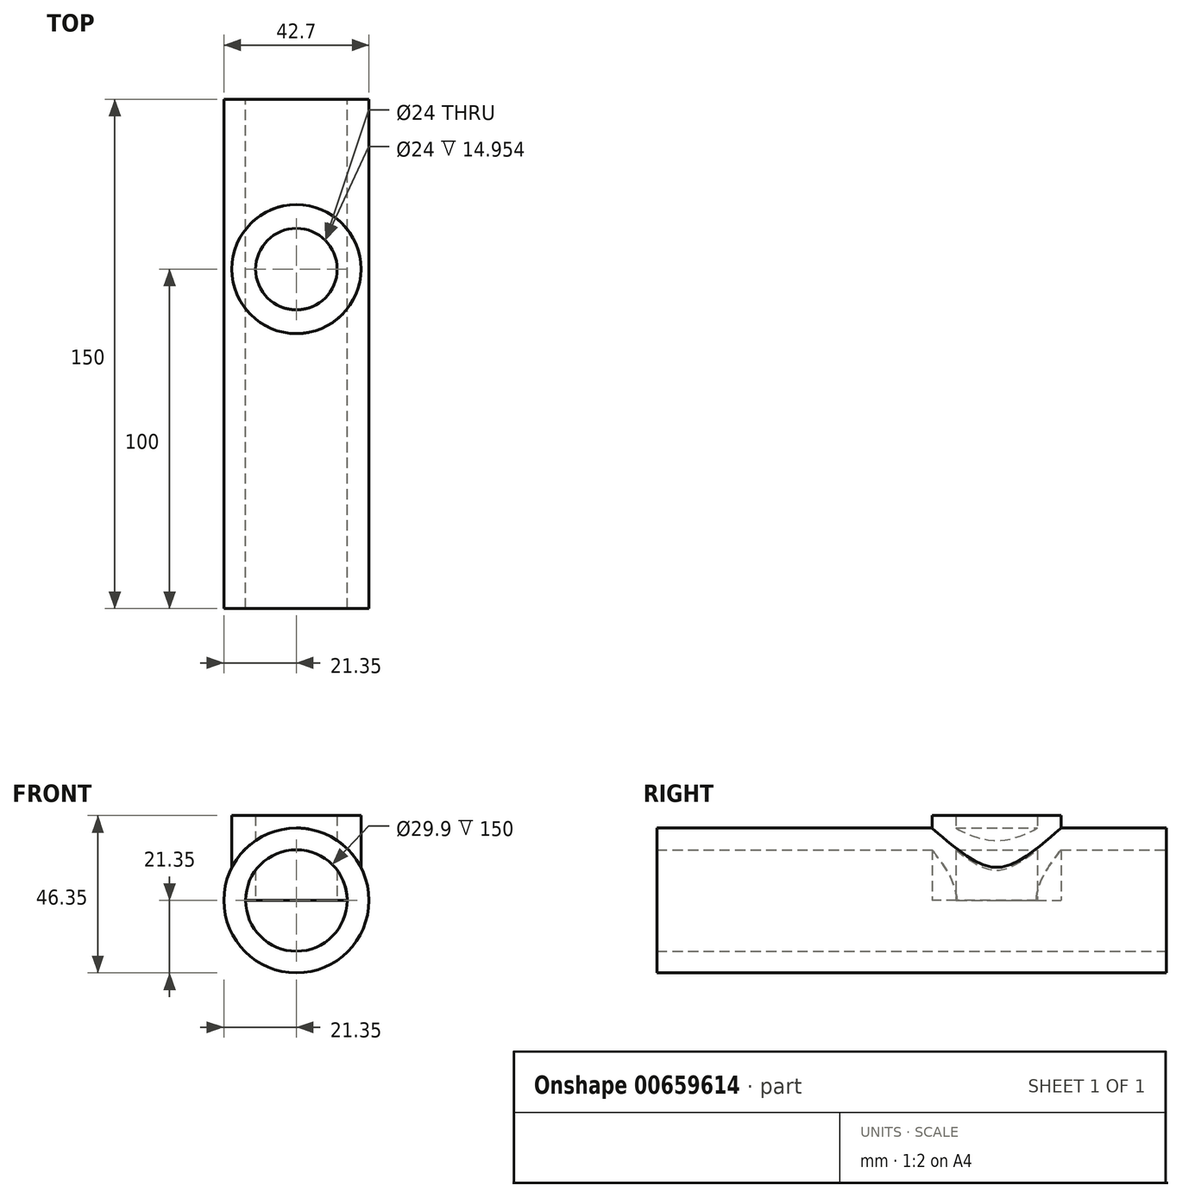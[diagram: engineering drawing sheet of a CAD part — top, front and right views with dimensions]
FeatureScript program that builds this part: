
annotation { "Feature Type Name" : "Feature", "Feature Type Description" : "" }
export const myFeature = defineFeature(function(context is Context, id is Id, definition is map)
    precondition{}
    {
        {
            var Q0;
            Q0=qCreatedBy(makeId("Front.planeOp"),FACE);
            var sketch = newSketch(context, id + "F0", { "sketchPlane" : qUnion([Q0])});
            skCircle(sketch, "E0", {"center": v(0, 0) * mm, "radius": 21.35 * mm});
            skCircle(sketch, "E1", {"center": v(0, 0) * mm, "radius": 14.95 * mm});
            skCircle(sketch, "E2", {"center": v(186.86, -2.46) * mm, "radius": 20.6 * mm});
            skSolve(sketch);
        }
        {
            var Q0;
            Q0=makeQuery(id+"F0.imprint","IMPRINT",FACE,{"disambiguationData":[TD([[makeQuery(id+"F0.imprint","IMPRINT",EDGE,{"derivedFrom":sQuery(id+"F0.wireOp",EDGE,"E0")}),1.0]])]});
            extrude(context, id + "F1", {"entities" : qUnion([Q0]), "depth" : 100 * mm, "offsetDistance" : 25 * mm});
        }
        {
            var Q0;
            Q0=makeQuery(id+"F1.opExtrude","CAP_FACE",FACE,{"disambiguationData":[OSD([sQuery(id+"F0.wireOp",EDGE,"E0"),sQuery(id+"F0.wireOp",EDGE,"E1")])],"isStart":true});
            extrude(context, id + "F2", {"entities" : qUnion([Q0]), "operationType" : NewBodyOperationType.ADD, "depth" : 50 * mm, "offsetDistance" : 25 * mm});
        }
        {
            var Q0;
            Q0=qCreatedBy(makeId("Top.planeOp"),FACE);
            var sketch = newSketch(context, id + "F3", { "sketchPlane" : qUnion([Q0])});
            skCircle(sketch, "E3", {"center": v(0, 0) * mm, "radius": 19 * mm});
            skCircle(sketch, "E4", {"center": v(0, 0) * mm, "radius": 12 * mm});
            skSolve(sketch);
        }
        {
            var Q0;
            Q0 = qSketchRegion(id + "F3", true);
            extrude(context, id + "F4", {"entities" : qUnion([Q0]), "operationType" : NewBodyOperationType.ADD, "depth" : 25 * mm, "offsetDistance" : 25 * mm});
        }
        {
            var Q0;
            Q0=makeQuery(id+"F1.opExtrude","SWEPT_BODY",BODY,{"disambiguationData":[OSD([sQuery(id+"F0.wireOp",EDGE,"E0"),sQuery(id+"F0.wireOp",EDGE,"E1")])]});
            transform(context, id + "F5", {"entities" : qUnion([Q0]), "transformType" : TransformType.TRANSLATION_3D, "dx" : 200 * mm, "dy" : 0 * mm, "dz" : 0 * mm, "makeCopy" : true});
        }
        {
            var Q0;
            Q0=makeQuery(id+"F5.opPattern","COPY",FACE,{"derivedFrom":makeQuery(id+"F1.opExtrude","CAP_FACE",FACE,{"disambiguationData":[OSD([sQuery(id+"F0.wireOp",EDGE,"E0"),sQuery(id+"F0.wireOp",EDGE,"E1")])],"isStart":false}),"instanceName":"1"});
            extrude(context, id + "F6", {"entities" : qUnion([Q0]), "operationType" : NewBodyOperationType.REMOVE, "endBound" : BoundingType.THROUGH_ALL, "oppositeDirection" : true, "depth" : 25 * mm, "offsetDistance" : 25 * mm});
        }
        {
            var Q0;
            Q0=makeQuery(id+"F6.boolean.opBoolean","SPLIT",BODY,{"disambiguationData":[OD(1.0)],"derivedFrom":makeQuery(id+"F5.opPattern","COPY",BODY,{"derivedFrom":makeQuery(id+"F1.opExtrude","SWEPT_BODY",BODY,{"disambiguationData":[OSD([sQuery(id+"F0.wireOp",EDGE,"E0"),sQuery(id+"F0.wireOp",EDGE,"E1")])]}),"instanceName":"1"})});
            deleteBodies(context, id + "F7", {"entities" : qUnion([Q0])});
        }
    });
